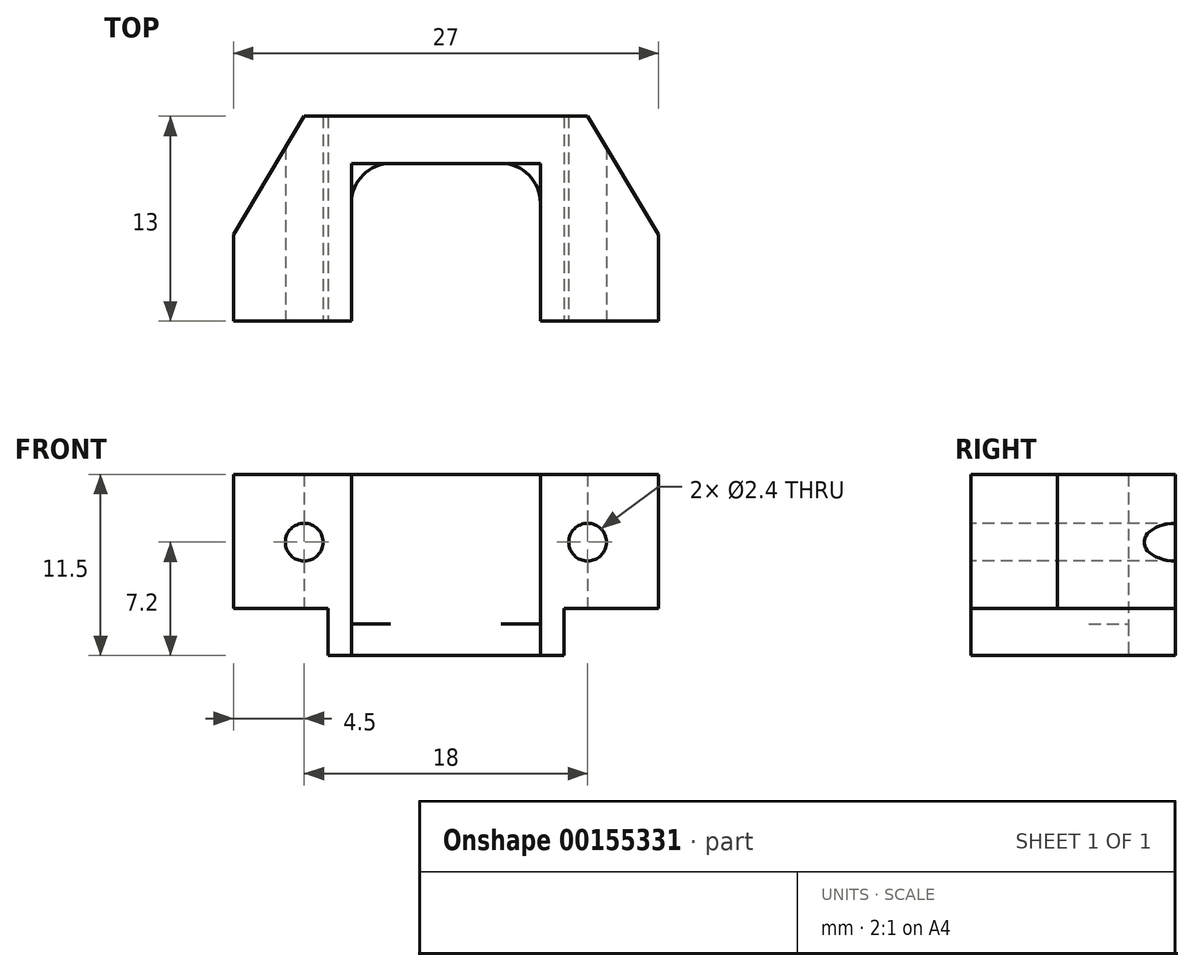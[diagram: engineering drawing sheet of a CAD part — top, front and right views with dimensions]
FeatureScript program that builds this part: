
annotation { "Feature Type Name" : "Feature", "Feature Type Description" : "" }
export const myFeature = defineFeature(function(context is Context, id is Id, definition is map)
    precondition{}
    {
        {
            var Q0;
            Q0=qCreatedBy(makeId("Top.planeOp"),FACE);
            var sketch = newSketch(context, id + "F0", { "sketchPlane" : qUnion([Q0])});
            skLineSegment(sketch, "E0", {"start": v(-13.5, 0) * mm, "end": v(-6, 0) * mm});
            skLineSegment(sketch, "E1", {"start": v(-6, 0) * mm, "end": v(-6, 10) * mm});
            skLineSegment(sketch, "E2", {"start": v(-6, 10) * mm, "end": v(6, 10) * mm});
            skLineSegment(sketch, "E3", {"start": v(6, 10) * mm, "end": v(6, 0) * mm});
            skLineSegment(sketch, "E4", {"start": v(6, 0) * mm, "end": v(13.5, 0) * mm});
            skLineSegment(sketch, "E5", {"start": v(13.5, 0) * mm, "end": v(13.5, 5.5) * mm});
            skLineSegment(sketch, "E6", {"start": v(9, 13) * mm, "end": v(-9, 13) * mm});
            skLineSegment(sketch, "E7", {"start": v(-13.5, 5.5) * mm, "end": v(-13.5, 0) * mm});
            skLineSegment(sketch, "E8", {"start": v(-13.5, 5.5) * mm, "end": v(-9, 13) * mm});
            skLineSegment(sketch, "E9", {"start": v(9, 13) * mm, "end": v(13.5, 5.5) * mm});
            skSolve(sketch);
        }
        {
            var Q0;
            Q0 = qSketchRegion(id + "F0", true);
            extrude(context, id + "F1", {"entities" : qUnion([Q0]), "depth" : 11.5 * mm});
        }
        {
            var Q0;
            Q0=makeQuery(id+"F1.opExtrude","SWEPT_FACE",FACE,{"disambiguationData":[OSD([sQuery(id+"F0.wireOp",EDGE,"E0")])]});
            var sketch = newSketch(context, id + "F2", { "sketchPlane" : qUnion([Q0])});
            skCircle(sketch, "E10", {"center": v(-9, 7.2) * mm, "radius": 1.2 * mm});
            skCircle(sketch, "E11", {"center": v(9, 7.2) * mm, "radius": 1.2 * mm});
            skLineSegment(sketch, "E12", {"start": v(-14.32, 7.2) * mm, "end": v(11.55, 7.2) * mm, "construction": true});
            skSolve(sketch);
        }
        {
            var Q0;
            Q0 = qSketchRegion(id + "F2", true);
            extrude(context, id + "F3", {"entities" : qUnion([Q0]), "operationType" : NewBodyOperationType.REMOVE, "oppositeDirection" : true, "depth" : 25 * mm});
        }
        {
            var Q0;
            Q0=makeQuery(id+"F1.opExtrude","SWEPT_EDGE",EDGE,{"disambiguationData":[OSD([sQuery(id+"F0.wireOp",EDGE,"E1"),sQuery(id+"F0.wireOp",EDGE,"E2")])]});
            var Q1;
            Q1=makeQuery(id+"F1.opExtrude","SWEPT_EDGE",EDGE,{"disambiguationData":[OSD([sQuery(id+"F0.wireOp",EDGE,"E2"),sQuery(id+"F0.wireOp",EDGE,"E3")])]});
            fillet(context, id + "F4", {"entities" : qUnion([Q0, Q1]), "radius" : 2.5 * mm, "tangentPropagation" : true, "allowEdgeOverflow" : false});
        }
        {
            var Q0;
            Q0=makeQuery(id+"F1.opExtrude","SWEPT_FACE",FACE,{"disambiguationData":[OSD([sQuery(id+"F0.wireOp",EDGE,"E2")])]});
            var sketch = newSketch(context, id + "F5", { "sketchPlane" : qUnion([Q0])});
            skLineSegment(sketch, "E13.bottom", {"start": v(-6, 11.5) * mm, "end": v(6, 11.5) * mm});
            skLineSegment(sketch, "E13.top", {"start": v(-6, 2) * mm, "end": v(6, 2) * mm});
            skLineSegment(sketch, "E13.left", {"start": v(-6, 11.5) * mm, "end": v(-6, 2) * mm});
            skLineSegment(sketch, "E14.trimOffspring", {"start": v(6, 11.5) * mm, "end": v(6, 2) * mm});
            skSolve(sketch);
        }
        {
            var Q0;
            Q0 = qSketchRegion(id + "F5", true);
            extrude(context, id + "F6", {"entities" : qUnion([Q0]), "operationType" : NewBodyOperationType.REMOVE, "endBound" : BoundingType.THROUGH_ALL, "depth" : 25 * mm});
        }
        {
            var Q0;
            Q0=makeQuery(id+"F1.opExtrude","SWEPT_FACE",FACE,{"disambiguationData":[OSD([sQuery(id+"F0.wireOp",EDGE,"E0")])]});
            var sketch = newSketch(context, id + "F7", { "sketchPlane" : qUnion([Q0])});
            skLineSegment(sketch, "E15.bottom", {"start": v(-13.5, 0) * mm, "end": v(-7.5, 0) * mm});
            skLineSegment(sketch, "E15.top", {"start": v(-13.5, 3) * mm, "end": v(-7.5, 3) * mm});
            skLineSegment(sketch, "E15.left", {"start": v(-13.5, 0) * mm, "end": v(-13.5, 3) * mm});
            skLineSegment(sketch, "E15.right", {"start": v(-7.5, 0) * mm, "end": v(-7.5, 3) * mm});
            skLineSegment(sketch, "E16.bottom", {"start": v(13.5, 0) * mm, "end": v(7.5, 0) * mm});
            skLineSegment(sketch, "E16.top", {"start": v(13.5, 3) * mm, "end": v(7.5, 3) * mm});
            skLineSegment(sketch, "E16.left", {"start": v(13.5, 0) * mm, "end": v(13.5, 3) * mm});
            skLineSegment(sketch, "E16.right", {"start": v(7.5, 0) * mm, "end": v(7.5, 3) * mm});
            skLineSegment(sketch, "E17", {"start": v(0, 0) * mm, "end": v(0, 11.49) * mm, "construction": true});
            skSolve(sketch);
        }
        {
            var Q0;
            Q0 = qSketchRegion(id + "F7", true);
            extrude(context, id + "F8", {"entities" : qUnion([Q0]), "operationType" : NewBodyOperationType.REMOVE, "endBound" : BoundingType.THROUGH_ALL, "oppositeDirection" : true, "depth" : 25 * mm});
        }
    });
